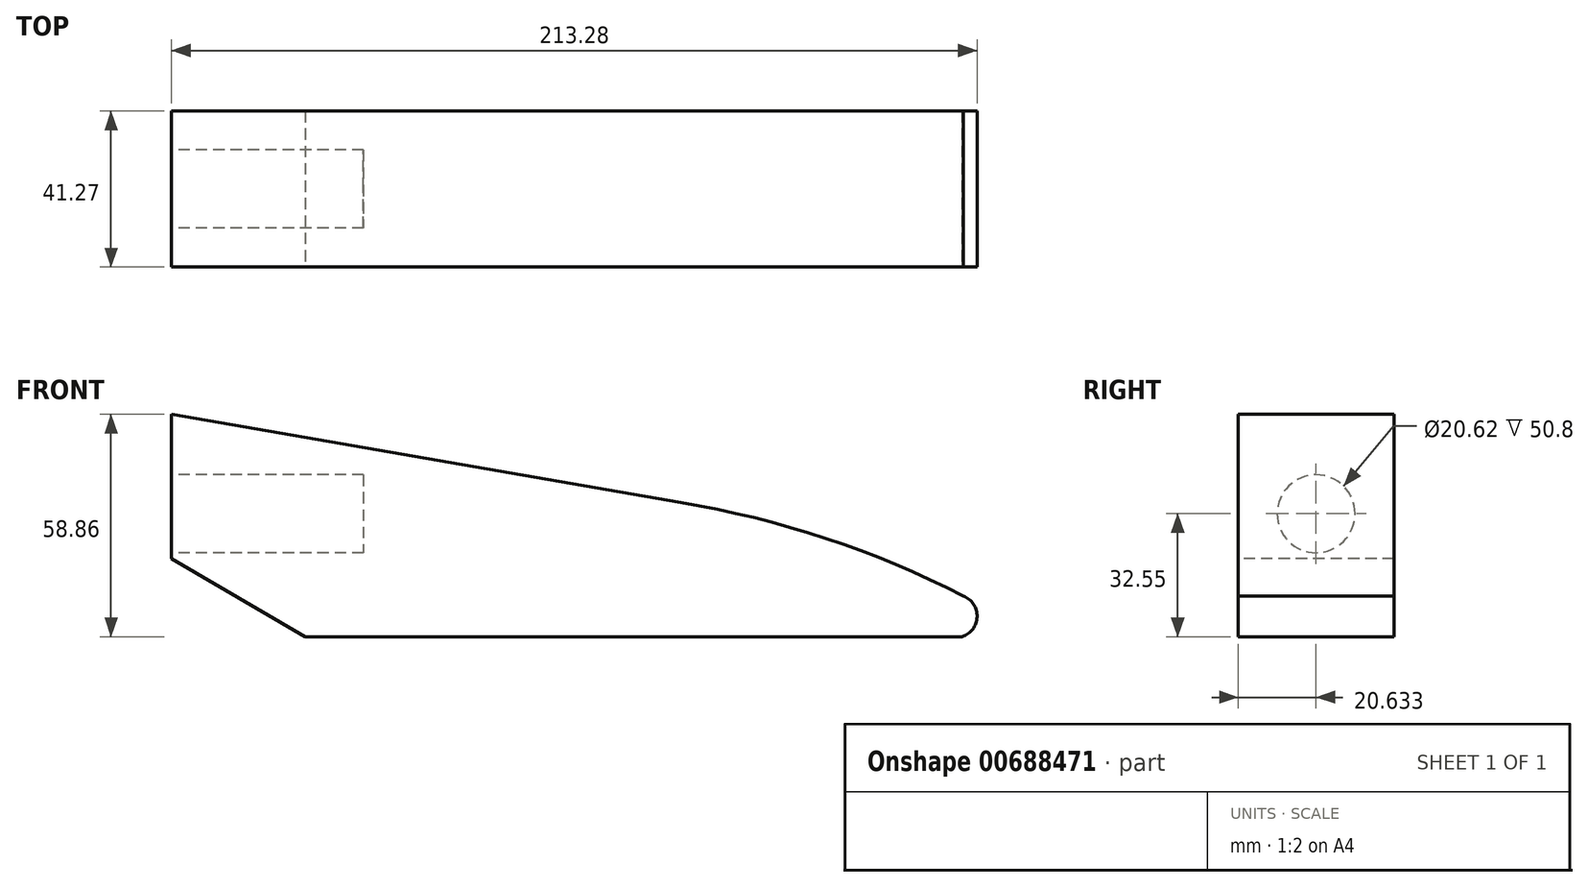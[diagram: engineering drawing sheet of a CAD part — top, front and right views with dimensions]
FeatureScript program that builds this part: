
annotation { "Feature Type Name" : "Feature", "Feature Type Description" : "" }
export const myFeature = defineFeature(function(context is Context, id is Id, definition is map)
    precondition{}
    {
        {
            var Q0;
            Q0=qCreatedBy(makeId("Front.planeOp"),FACE);
            var sketch = newSketch(context, id + "F0", { "sketchPlane" : qUnion([Q0])});
            skLineSegment(sketch, "E0", {"start": v(0, 0) * mm, "end": v(0, 71.44) * mm});
            skLineSegment(sketch, "E1", {"start": v(0, 0) * mm, "end": v(304.8, 0) * mm});
            skLineSegment(sketch, "E2", {"start": v(304.8, 0) * mm, "end": v(304.8, 15.88) * mm});
            skLineSegment(sketch, "E3", {"start": v(0, 71.44) * mm, "end": v(304.8, 15.88) * mm});
            skSolve(sketch);
        }
        {
            var Q0;
            Q0=makeQuery(id+"F0.imprint","IMPRINT",FACE,{"disambiguationData":[TD([[makeQuery(id+"F0.imprint","IMPRINT",EDGE,{"derivedFrom":sQuery(id+"F0.wireOp",EDGE,"E0")}),-1.0]])]});
            extrude(context, id + "F1", {"entities" : qUnion([Q0]), "depth" : 41.27 * mm, "offsetDistance" : 25.4 * mm});
        }
        {
            var Q0;
            Q0=makeQuery(id+"F1.opExtrude","SWEPT_FACE",FACE,{"disambiguationData":[OSD([sQuery(id+"F0.wireOp",EDGE,"E0")])]});
            var sketch = newSketch(context, id + "F2", { "sketchPlane" : qUnion([Q0])});
            skPoint(sketch, "E4.endSnap0", {"position": v(20.64, 71.44) * mm});
            skCircle(sketch, "E5", {"center": v(20.64, 32.55) * mm, "radius": 10.31 * mm});
            skSolve(sketch);
        }
        {
            var Q0;
            Q0=makeQuery(id+"F2.imprint","IMPRINT",FACE,{"disambiguationData":[TD([[makeQuery(id+"F2.imprint","IMPRINT",EDGE,{"derivedFrom":sQuery(id+"F2.wireOp",EDGE,"E5")}),1.0]])]});
            extrude(context, id + "F3", {"entities" : qUnion([Q0]), "operationType" : NewBodyOperationType.REMOVE, "oppositeDirection" : true, "depth" : 50.8 * mm, "offsetDistance" : 25.4 * mm});
        }
        {
            var Q0;
            Q0=makeQuery(id+"F1.opExtrude","CAP_FACE",FACE,{"disambiguationData":[OSD([sQuery(id+"F0.wireOp",EDGE,"E0"),sQuery(id+"F0.wireOp",EDGE,"E1"),sQuery(id+"F0.wireOp",EDGE,"E2"),sQuery(id+"F0.wireOp",EDGE,"E3")])],"isStart":false});
            var sketch = newSketch(context, id + "F4", { "sketchPlane" : qUnion([Q0])});
            skPoint(sketch, "E6.orphan", {"position": v(228.6, 0) * mm});
            skArc(sketch, "E7", {"start": v(209.62, 10.78) * mm, "mid": v(105.96, 38.64) * mm, "end": v(0, 21.55) * mm});
            skArc(sketch, "E8", {"start": v(209.3, 0) * mm, "mid": v(213.28, 5.28) * mm, "end": v(209.62, 10.78) * mm});
            skLineSegment(sketch, "E9", {"start": v(35.43, 0) * mm, "end": v(58.29, 0) * mm});
            skLineSegment(sketch, "E10", {"start": v(58.29, 0) * mm, "end": v(58.29, 7.62) * mm});
            skLineSegment(sketch, "E11", {"start": v(58.29, 0) * mm, "end": v(172.59, 0) * mm});
            skLineSegment(sketch, "E12", {"start": v(172.59, 0) * mm, "end": v(172.59, 5.08) * mm});
            skLineSegment(sketch, "E13", {"start": v(58.47, -11.43) * mm, "end": v(172.66, -10.92) * mm});
            skLineSegment(sketch, "E14", {"start": v(0, 52.18) * mm, "end": v(0, 21.55) * mm});
            skLineSegment(sketch, "E15", {"start": v(0, 20.68) * mm, "end": v(35.43, 0) * mm});
            skCircle(sketch, "E16", {"center": v(58.29, 7.62) * mm, "radius": 1.65 * mm});
            skCircle(sketch, "E17", {"center": v(172.59, 5.08) * mm, "radius": 1.65 * mm});
            skLineSegment(sketch, "E18", {"start": v(138.27, 34.9) * mm, "end": v(0, 58.86) * mm});
            skSolve(sketch);
        }
        {
            var Q0;
            {var subQ0=sQuery(id+"F4.wireOp",EDGE,"E15");Q0=makeQuery(id+"F4.imprint","IMPRINT",FACE,{"disambiguationData":[TD([[makeQuery(id+"F4.imprint","IMPRINT",EDGE,{"derivedFrom":subQ0}),-1.0]])]});}
            var Q1;
            {var subQ0=sQuery(id+"F4.wireOp",EDGE,"E8");Q1=makeQuery(id+"F4.imprint","IMPRINT",FACE,{"disambiguationData":[TD([[makeQuery(id+"F4.imprint","IMPRINT",EDGE,{"derivedFrom":subQ0}),-1.0]])]});}
            extrude(context, id + "F5", {"entities" : qUnion([Q0, Q1]), "operationType" : NewBodyOperationType.REMOVE, "endBound" : BoundingType.THROUGH_ALL, "oppositeDirection" : true, "depth" : 25.4 * mm, "offsetDistance" : 25.4 * mm});
        }
    });
